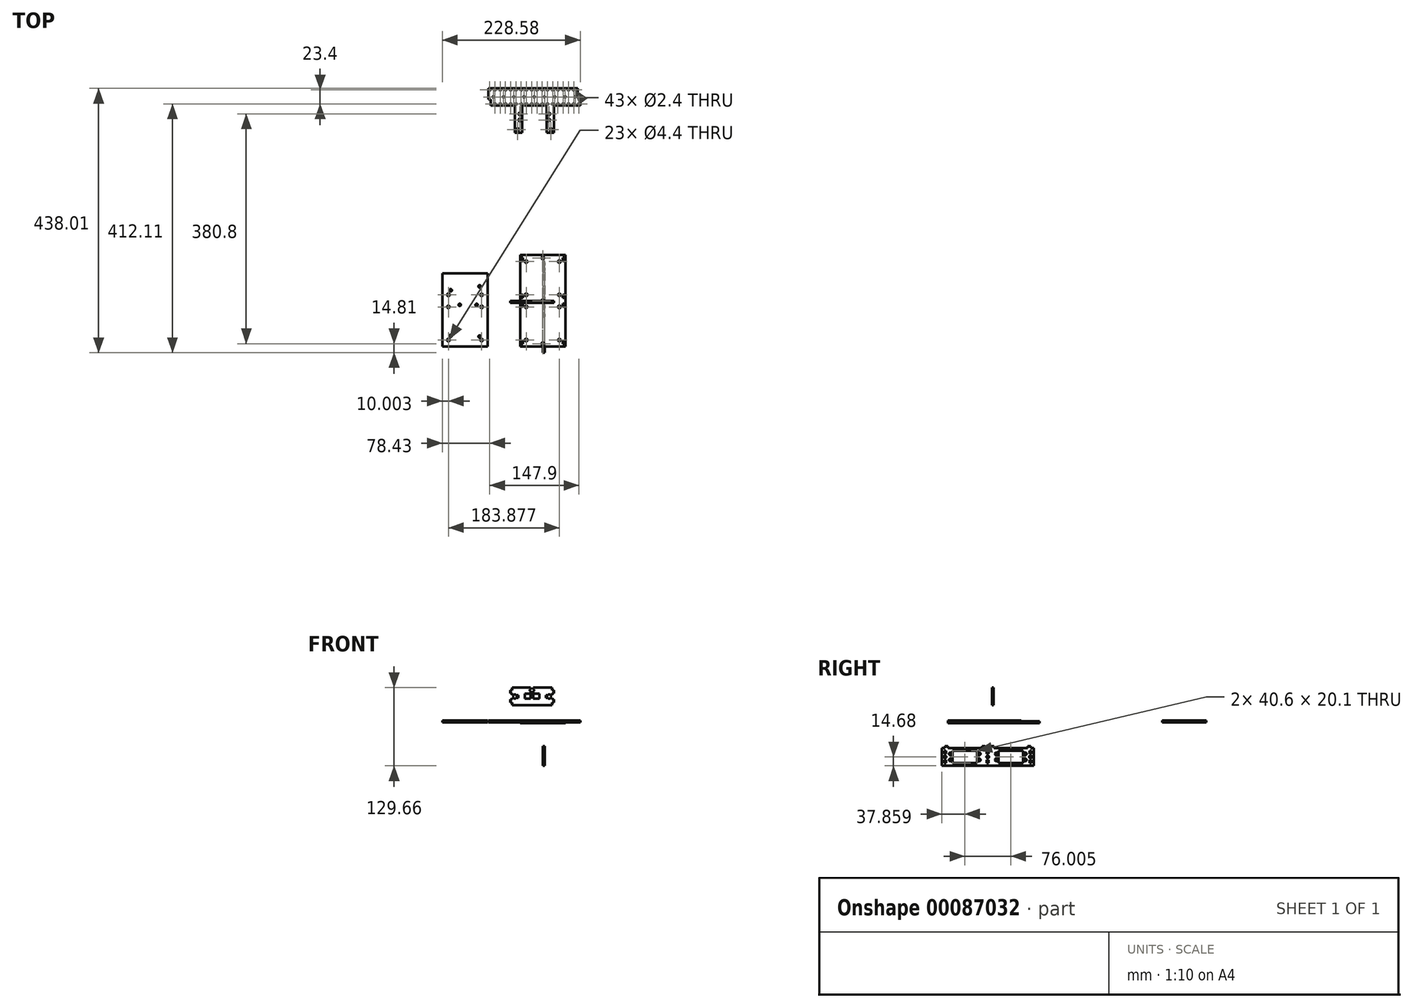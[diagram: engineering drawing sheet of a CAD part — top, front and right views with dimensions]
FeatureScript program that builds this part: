
annotation { "Feature Type Name" : "Feature", "Feature Type Description" : "" }
export const myFeature = defineFeature(function(context is Context, id is Id, definition is map)
    precondition{}
    {
        {
            assignVariable(context, id + "F0", {"name" : "Mat_Thickness", "anyValue" : 3});
        }
        {
            var Q0;
            Q0=qCreatedBy(makeId("Top.planeOp"),FACE);
            var sketch = newSketch(context, id + "F1", { "sketchPlane" : qUnion([Q0])});
            skLineSegment(sketch, "E0.bottom", {"start": v(-37.5, 76) * mm, "end": v(37.5, 76) * mm});
            skLineSegment(sketch, "E0.top", {"start": v(-37.5, -76) * mm, "end": v(37.5, -76) * mm});
            skLineSegment(sketch, "E0.left", {"start": v(-37.5, 76) * mm, "end": v(-37.5, -76) * mm});
            skLineSegment(sketch, "E0.right", {"start": v(37.5, 76) * mm, "end": v(37.5, -76) * mm});
            skLineSegment(sketch, "E1", {"start": v(-37.5, -76) * mm, "end": v(37.5, 76) * mm, "construction": true});
            skLineSegment(sketch, "E2", {"start": v(-37.5, 76) * mm, "end": v(37.5, -76) * mm, "construction": true});
            skSolve(sketch);
        }
        {
            var Q0;
            Q0=makeQuery(id+"F1.imprint","IMPRINT",FACE,{"disambiguationData":[TD([[makeQuery(id+"F1.imprint","IMPRINT",EDGE,{"derivedFrom":sQuery(id+"F1.wireOp",EDGE,"E0.bottom")}),-1.0]])]});
            extrude(context, id + "F2", {"entities" : qUnion([Q0]), "endBound" : BoundingType.SYMMETRIC, "depth" : 3 * mm});
        }
        {
            var Q0;
            Q0=makeQuery(id+"F2.opExtrude","CAP_FACE",FACE,{"disambiguationData":[OSD([sQuery(id+"F1.wireOp",EDGE,"E0.bottom"),sQuery(id+"F1.wireOp",EDGE,"E0.top"),sQuery(id+"F1.wireOp",EDGE,"E0.left"),sQuery(id+"F1.wireOp",EDGE,"E0.right")])],"isStart":false});
            var sketch = newSketch(context, id + "F3", { "sketchPlane" : qUnion([Q0])});
            skPoint(sketch, "E3", {"position": v(-27.5, -71) * mm});
            skPoint(sketch, "E4", {"position": v(27.5, -71) * mm});
            skPoint(sketch, "E5", {"position": v(27.5, 71) * mm});
            skPoint(sketch, "E6", {"position": v(-27.5, 71) * mm});
            skLineSegment(sketch, "E7", {"start": v(-27.5, -71) * mm, "end": v(-27.5, 0) * mm, "construction": true});
            skLineSegment(sketch, "E8", {"start": v(-27.5, 0) * mm, "end": v(-27.5, 71) * mm, "construction": true});
            skLineSegment(sketch, "E9", {"start": v(-27.5, 71) * mm, "end": v(27.5, 71) * mm, "construction": true});
            skLineSegment(sketch, "E10", {"start": v(27.5, 71) * mm, "end": v(27.5, 0) * mm, "construction": true});
            skLineSegment(sketch, "E11", {"start": v(27.5, 0) * mm, "end": v(27.5, -71) * mm, "construction": true});
            skLineSegment(sketch, "E12", {"start": v(27.5, -71) * mm, "end": v(-27.5, -71) * mm, "construction": true});
            skLineSegment(sketch, "E13", {"start": v(-27.5, 0) * mm, "end": v(27.5, 0) * mm, "construction": true});
            skPoint(sketch, "E14", {"position": v(0, 0) * mm});
            skPoint(sketch, "E15", {"position": v(0, 71) * mm});
            skPoint(sketch, "E16", {"position": v(0, -71) * mm});
            skLineSegment(sketch, "E17", {"start": v(27.5, -10) * mm, "end": v(-27.5, -10) * mm, "construction": true});
            skLineSegment(sketch, "E18", {"start": v(27.5, 10) * mm, "end": v(-27.5, 10) * mm, "construction": true});
            skPoint(sketch, "E19", {"position": v(27.5, -10) * mm});
            skPoint(sketch, "E20", {"position": v(27.5, 10) * mm});
            skPoint(sketch, "E21", {"position": v(-27.5, 10) * mm});
            skPoint(sketch, "E22", {"position": v(-27.5, -10) * mm});
            skLineSegment(sketch, "E23.bottom", {"start": v(-27.5, -65) * mm, "end": v(27.5, -65) * mm, "construction": true});
            skLineSegment(sketch, "E23.top", {"start": v(-27.5, 65) * mm, "end": v(27.5, 65) * mm, "construction": true});
            skLineSegment(sketch, "E23.left", {"start": v(-27.5, -65) * mm, "end": v(-27.5, 65) * mm, "construction": true});
            skLineSegment(sketch, "E23.right", {"start": v(27.5, -65) * mm, "end": v(27.5, 65) * mm, "construction": true});
            skSolve(sketch);
        }
        {
            var Q0;
            Q0=sQuery(id+"F3.wireOp",VERTEX,"E14");
            var Q1;
            Q1=sQuery(id+"F3.wireOp",VERTEX,"E15");
            var Q2;
            Q2=sQuery(id+"F3.wireOp",VERTEX,"E16");
            var Q3;
            Q3=sQuery(id+"F3.wireOp",VERTEX,"E20");
            var Q4;
            Q4=sQuery(id+"F3.wireOp",VERTEX,"E19");
            var Q5;
            Q5=sQuery(id+"F3.wireOp",VERTEX,"E22");
            var Q6;
            Q6=sQuery(id+"F3.wireOp",VERTEX,"E21");
            var Q7;
            Q7=sQuery(id+"F3.wireOp",VERTEX,"E23.left.end");
            var Q8;
            Q8=sQuery(id+"F3.wireOp",VERTEX,"E23.right.end");
            var Q9;
            Q9=sQuery(id+"F3.wireOp",VERTEX,"E23.bottom.start");
            var Q10;
            Q10=sQuery(id+"F3.wireOp",VERTEX,"E23.right.start");
            var Q11;
            Q11=makeQuery(id+"F2.opExtrude","SWEPT_BODY",BODY,{"disambiguationData":[OSD([sQuery(id+"F1.wireOp",EDGE,"E0.bottom"),sQuery(id+"F1.wireOp",EDGE,"E0.top"),sQuery(id+"F1.wireOp",EDGE,"E0.left"),sQuery(id+"F1.wireOp",EDGE,"E0.right")])]});
            hole(context, id + "F4", {"style" : HoleStyle.SIMPLE, "endStyle" : HoleEndStyle.THROUGH, "standardTappedOrClearance" : lookupTablePath({ "standard" : "ISO", "fit" : "Normal", "size" : "M4", "type" : "Clearance" }), "standardBlindInLast" : lookupTablePath({ "fit" : "Standard", "standard" : "ISO", "size" : "M4", "type" : "Clearance" }), "holeDiameter" : 4.4 * mm, "locations" : qUnion([Q0, Q1, Q2, Q3, Q4, Q5, Q6, Q7, Q8, Q9, Q10]), "scope" : qUnion([Q11]), "isTappedThrough" : true});
        }
        {
            var Q0;
            Q0=qCreatedBy(makeId("Right.planeOp"),FACE);
            var sketch = newSketch(context, id + "F5", { "sketchPlane" : qUnion([Q0])});
            skLineSegment(sketch, "E24.bottom", {"start": v(-85.81, -72.16) * mm, "end": v(66.19, -72.16) * mm});
            skLineSegment(sketch, "E24.left", {"start": v(-85.81, -72.16) * mm, "end": v(-85.81, -42.8) * mm});
            skLineSegment(sketch, "E24.right", {"start": v(66.19, -72.16) * mm, "end": v(66.19, -42.8) * mm});
            skLineSegment(sketch, "E25", {"start": v(-85.81, -42.8) * mm, "end": v(-81.11, -42.8) * mm});
            skLineSegment(sketch, "E26", {"start": v(-81.11, -42.8) * mm, "end": v(-81.11, -39.8) * mm});
            skLineSegment(sketch, "E27", {"start": v(-81.11, -39.8) * mm, "end": v(-75.91, -39.8) * mm});
            skLineSegment(sketch, "E28", {"start": v(-75.91, -39.8) * mm, "end": v(-75.91, -42.8) * mm});
            skLineSegment(sketch, "E29", {"start": v(-75.91, -42.8) * mm, "end": v(-19.71, -42.8) * mm});
            skLineSegment(sketch, "E30", {"start": v(-19.71, -42.8) * mm, "end": v(-19.71, -39.8) * mm});
            skLineSegment(sketch, "E31", {"start": v(-19.71, -39.8) * mm, "end": v(-14.51, -39.8) * mm});
            skLineSegment(sketch, "E32", {"start": v(-14.51, -39.8) * mm, "end": v(-14.51, -42.8) * mm});
            skLineSegment(sketch, "E33", {"start": v(-14.51, -42.8) * mm, "end": v(-5.11, -42.8) * mm});
            skLineSegment(sketch, "E34", {"start": v(-5.11, -42.8) * mm, "end": v(-5.11, -39.8) * mm});
            skLineSegment(sketch, "E35", {"start": v(-5.11, -39.8) * mm, "end": v(0.09, -39.8) * mm});
            skLineSegment(sketch, "E36", {"start": v(0.09, -39.8) * mm, "end": v(0.09, -42.8) * mm});
            skLineSegment(sketch, "E37", {"start": v(0.09, -42.8) * mm, "end": v(56.29, -42.8) * mm});
            skLineSegment(sketch, "E38", {"start": v(56.29, -42.8) * mm, "end": v(56.29, -39.8) * mm});
            skLineSegment(sketch, "E39", {"start": v(56.29, -39.8) * mm, "end": v(61.49, -39.8) * mm});
            skLineSegment(sketch, "E40", {"start": v(61.49, -39.8) * mm, "end": v(61.49, -42.8) * mm});
            skLineSegment(sketch, "E41", {"start": v(61.49, -42.8) * mm, "end": v(66.19, -42.8) * mm});
            skPoint(sketch, "E42", {"position": v(-9.95, -72.16) * mm});
            skPoint(sketch, "E42.positionSnap0", {"position": v(-9.81, -72.16) * mm});
            skLineSegment(sketch, "E43", {"start": v(-9.95, -72.16) * mm, "end": v(-9.95, -42.8) * mm, "construction": true});
            skLineSegment(sketch, "E44.bottom", {"start": v(-68.25, -47.43) * mm, "end": v(-27.65, -47.43) * mm});
            skLineSegment(sketch, "E44.top", {"start": v(-68.25, -67.53) * mm, "end": v(-27.65, -67.53) * mm});
            skLineSegment(sketch, "E44.left", {"start": v(-68.25, -47.43) * mm, "end": v(-68.25, -67.53) * mm});
            skLineSegment(sketch, "E44.right", {"start": v(-27.65, -47.43) * mm, "end": v(-27.65, -67.53) * mm});
            skCircle(sketch, "E45", {"center": v(-71.95, -52.48) * mm, "radius": 2.2 * mm});
            skCircle(sketch, "E46", {"center": v(-23.95, -52.48) * mm, "radius": 2.2 * mm});
            skCircle(sketch, "E47", {"center": v(-23.95, -62.48) * mm, "radius": 2.2 * mm});
            skCircle(sketch, "E48", {"center": v(-71.95, -62.48) * mm, "radius": 2.2 * mm});
            skLineSegment(sketch, "E49.bottom", {"start": v(-71.95, -52.48) * mm, "end": v(-23.95, -52.48) * mm, "construction": true});
            skLineSegment(sketch, "E49.top", {"start": v(-71.95, -62.48) * mm, "end": v(-23.95, -62.48) * mm, "construction": true});
            skLineSegment(sketch, "E49.left", {"start": v(-71.95, -52.48) * mm, "end": v(-71.95, -62.48) * mm, "construction": true});
            skLineSegment(sketch, "E49.right", {"start": v(-23.95, -52.48) * mm, "end": v(-23.95, -62.48) * mm, "construction": true});
            skCircle(sketch, "E50.MirrorC", {"center": v(4.05, -52.48) * mm, "radius": 2.2 * mm});
            skCircle(sketch, "E51.MirrorC", {"center": v(4.05, -62.48) * mm, "radius": 2.2 * mm});
            skLineSegment(sketch, "E52.MirrorCS", {"start": v(7.75, -47.43) * mm, "end": v(7.75, -67.53) * mm});
            skLineSegment(sketch, "E53.MirrorCS", {"start": v(48.35, -47.43) * mm, "end": v(7.75, -47.43) * mm});
            skLineSegment(sketch, "E54.MirrorCS", {"start": v(48.35, -47.43) * mm, "end": v(48.35, -67.53) * mm});
            skLineSegment(sketch, "E55.MirrorCS", {"start": v(48.35, -67.53) * mm, "end": v(7.75, -67.53) * mm});
            skCircle(sketch, "E56.MirrorC", {"center": v(52.05, -62.48) * mm, "radius": 2.2 * mm});
            skCircle(sketch, "E57.MirrorC", {"center": v(52.05, -52.48) * mm, "radius": 2.2 * mm});
            skCircle(sketch, "E58", {"center": v(-9.95, -57.48) * mm, "radius": 2.2 * mm});
            skLineSegment(sketch, "E59.bottom", {"start": v(-11.45, -52.48) * mm, "end": v(-8.45, -52.48) * mm});
            skLineSegment(sketch, "E59.top", {"start": v(-11.45, -47.18) * mm, "end": v(-8.45, -47.18) * mm});
            skLineSegment(sketch, "E59.left", {"start": v(-11.45, -52.48) * mm, "end": v(-11.45, -47.18) * mm});
            skLineSegment(sketch, "E59.right", {"start": v(-8.45, -52.48) * mm, "end": v(-8.45, -47.18) * mm});
            skPoint(sketch, "E59.middle", {"position": v(-9.95, -49.83) * mm});
            skLineSegment(sketch, "E60.bottom", {"start": v(-11.45, -67.78) * mm, "end": v(-8.45, -67.78) * mm});
            skLineSegment(sketch, "E60.top", {"start": v(-11.45, -62.48) * mm, "end": v(-8.45, -62.48) * mm});
            skLineSegment(sketch, "E60.left", {"start": v(-11.45, -67.78) * mm, "end": v(-11.45, -62.48) * mm});
            skLineSegment(sketch, "E60.right", {"start": v(-8.45, -67.78) * mm, "end": v(-8.45, -62.48) * mm});
            skPoint(sketch, "E60.middle", {"position": v(-9.95, -65.13) * mm});
            skLineSegment(sketch, "E61.bottom", {"start": v(62.42, -47.18) * mm, "end": v(59.42, -47.18) * mm});
            skLineSegment(sketch, "E61.top", {"start": v(62.42, -52.48) * mm, "end": v(59.42, -52.48) * mm});
            skLineSegment(sketch, "E61.left", {"start": v(62.42, -47.18) * mm, "end": v(62.42, -52.48) * mm});
            skLineSegment(sketch, "E61.right", {"start": v(59.42, -47.18) * mm, "end": v(59.42, -52.48) * mm});
            skLineSegment(sketch, "E62.bottom", {"start": v(62.42, -67.78) * mm, "end": v(59.42, -67.78) * mm});
            skLineSegment(sketch, "E62.top", {"start": v(62.42, -62.48) * mm, "end": v(59.42, -62.48) * mm});
            skLineSegment(sketch, "E62.left", {"start": v(62.42, -67.78) * mm, "end": v(62.42, -62.48) * mm});
            skLineSegment(sketch, "E62.right", {"start": v(59.42, -67.78) * mm, "end": v(59.42, -62.48) * mm});
            skLineSegment(sketch, "E63", {"start": v(66.19, -57.48) * mm, "end": v(-85.81, -57.48) * mm, "construction": true});
            skPoint(sketch, "E64", {"position": v(48.35, -57.48) * mm});
            skLineSegment(sketch, "E65", {"start": v(-68.25, -67.53) * mm, "end": v(-27.65, -47.43) * mm, "construction": true});
            skPoint(sketch, "E66", {"position": v(-47.95, -57.48) * mm});
            skCircle(sketch, "E67", {"center": v(60.92, -57.48) * mm, "radius": 2.2 * mm});
            skPoint(sketch, "E67.centerSnap0", {"position": v(60.92, -52.48) * mm});
            skCircle(sketch, "E68.MirrorC", {"center": v(-80.81, -57.48) * mm, "radius": 2.2 * mm});
            skLineSegment(sketch, "E69.MirrorCS", {"start": v(-82.31, -52.48) * mm, "end": v(-79.31, -52.48) * mm});
            skLineSegment(sketch, "E70.MirrorCS", {"start": v(-82.31, -47.18) * mm, "end": v(-79.31, -47.18) * mm});
            skLineSegment(sketch, "E71.MirrorCS", {"start": v(-82.31, -47.18) * mm, "end": v(-82.31, -52.48) * mm});
            skLineSegment(sketch, "E72.MirrorCS", {"start": v(-79.31, -47.18) * mm, "end": v(-79.31, -52.48) * mm});
            skLineSegment(sketch, "E73.MirrorCS", {"start": v(-82.31, -67.78) * mm, "end": v(-82.31, -62.48) * mm});
            skLineSegment(sketch, "E74.MirrorCS", {"start": v(-82.31, -62.48) * mm, "end": v(-79.31, -62.48) * mm});
            skLineSegment(sketch, "E75.MirrorCS", {"start": v(-86.08, -57.48) * mm, "end": v(65.92, -57.48) * mm, "construction": true});
            skLineSegment(sketch, "E76.MirrorCS", {"start": v(-79.31, -67.78) * mm, "end": v(-79.31, -62.48) * mm});
            skLineSegment(sketch, "E77.MirrorCS", {"start": v(-82.31, -67.78) * mm, "end": v(-79.31, -67.78) * mm});
            skLineSegment(sketch, "E78.bottom", {"start": v(52.05, -52.48) * mm, "end": v(4.05, -52.48) * mm, "construction": true});
            skLineSegment(sketch, "E78.top", {"start": v(52.05, -62.48) * mm, "end": v(4.05, -62.48) * mm, "construction": true});
            skLineSegment(sketch, "E78.left", {"start": v(52.05, -52.48) * mm, "end": v(52.05, -62.48) * mm, "construction": true});
            skLineSegment(sketch, "E78.right", {"start": v(4.05, -52.48) * mm, "end": v(4.05, -62.48) * mm, "construction": true});
            skPoint(sketch, "E79", {"position": v(-71.95, -57.48) * mm});
            skLineSegment(sketch, "E80", {"start": v(28.05, -52.48) * mm, "end": v(28.05, -62.48) * mm, "construction": true});
            skLineSegment(sketch, "E81", {"start": v(-47.95, -52.48) * mm, "end": v(-47.95, -57.48) * mm, "construction": true});
            skSolve(sketch);
        }
        {
            var Q0;
            Q0 = qSketchRegion(id + "F5", true);
            extrude(context, id + "F6", {"entities" : qUnion([Q0]), "depth" : (getVariable(context, 'Mat_Thickness')) * mm});
        }
        {
            var Q0;
            Q0=qCreatedBy(makeId("Front.planeOp"),FACE);
            var sketch = newSketch(context, id + "F7", { "sketchPlane" : qUnion([Q0])});
            skLineSegment(sketch, "E82", {"start": v(-50.74, 45.02) * mm, "end": v(-47.74, 45.02) * mm});
            skLineSegment(sketch, "E83", {"start": v(-47.74, 45.02) * mm, "end": v(-47.74, 46.32) * mm});
            skLineSegment(sketch, "E84", {"start": v(-47.74, 46.32) * mm, "end": v(-44.74, 46.32) * mm});
            skLineSegment(sketch, "E85", {"start": v(-44.74, 46.32) * mm, "end": v(-44.74, 45.02) * mm});
            skLineSegment(sketch, "E86", {"start": v(-44.74, 45.02) * mm, "end": v(-40.74, 45.02) * mm});
            skLineSegment(sketch, "E87", {"start": v(-40.74, 45.02) * mm, "end": v(-40.74, 40.62) * mm});
            skLineSegment(sketch, "E88", {"start": v(-40.74, 40.62) * mm, "end": v(-44.74, 40.62) * mm});
            skLineSegment(sketch, "E89", {"start": v(-44.74, 40.62) * mm, "end": v(-44.74, 39.32) * mm});
            skLineSegment(sketch, "E90", {"start": v(-44.74, 39.32) * mm, "end": v(-47.74, 39.32) * mm});
            skLineSegment(sketch, "E91", {"start": v(-47.74, 39.32) * mm, "end": v(-47.74, 40.62) * mm});
            skLineSegment(sketch, "E92", {"start": v(-47.74, 40.62) * mm, "end": v(-50.74, 40.62) * mm});
            skLineSegment(sketch, "E93", {"start": v(-17.74, 57.5) * mm, "end": v(-17.74, 28.15) * mm, "construction": true});
            skLineSegment(sketch, "E94", {"start": v(-50.74, 28.15) * mm, "end": v(-17.74, 28.15) * mm});
            skLineSegment(sketch, "E95", {"start": v(-50.74, 57.5) * mm, "end": v(-50.74, 53.07) * mm});
            skLineSegment(sketch, "E96", {"start": v(-50.74, 28.15) * mm, "end": v(-50.74, 32.57) * mm});
            skLineSegment(sketch, "E97", {"start": v(-19.94, 48.5) * mm, "end": v(-19.94, 51.5) * mm});
            skLineSegment(sketch, "E98", {"start": v(-19.94, 51.5) * mm, "end": v(-21.24, 51.5) * mm});
            skLineSegment(sketch, "E99", {"start": v(-21.24, 51.5) * mm, "end": v(-21.24, 54.5) * mm});
            skLineSegment(sketch, "E100", {"start": v(-21.24, 54.5) * mm, "end": v(-19.94, 54.5) * mm});
            skLineSegment(sketch, "E101", {"start": v(-19.94, 54.5) * mm, "end": v(-19.94, 57.5) * mm});
            skLineSegment(sketch, "E102", {"start": v(-50.74, 57.5) * mm, "end": v(-19.94, 57.5) * mm});
            skLineSegment(sketch, "E103", {"start": v(-19.94, 48.5) * mm, "end": v(-17.74, 48.5) * mm});
            skLineSegment(sketch, "E104", {"start": v(-50.74, 45.02) * mm, "end": v(-50.74, 40.62) * mm, "construction": true});
            skLineSegment(sketch, "E105", {"start": v(-40.74, 42.82) * mm, "end": v(-50.74, 42.82) * mm, "construction": true});
            skLineSegment(sketch, "E106", {"start": v(-50.74, 47.87) * mm, "end": v(-53.74, 47.87) * mm});
            skLineSegment(sketch, "E107", {"start": v(-53.74, 47.87) * mm, "end": v(-53.74, 53.07) * mm});
            skLineSegment(sketch, "E108", {"start": v(-53.74, 53.07) * mm, "end": v(-50.74, 53.07) * mm});
            skLineSegment(sketch, "E109.trimOffspring", {"start": v(-50.74, 47.87) * mm, "end": v(-50.74, 45.02) * mm});
            skLineSegment(sketch, "E110", {"start": v(-50.74, 37.77) * mm, "end": v(-53.74, 37.77) * mm});
            skLineSegment(sketch, "E111", {"start": v(-53.74, 37.77) * mm, "end": v(-53.74, 32.57) * mm});
            skLineSegment(sketch, "E112", {"start": v(-53.74, 32.57) * mm, "end": v(-50.74, 32.57) * mm});
            skLineSegment(sketch, "E113.trimOffspring", {"start": v(-50.74, 37.77) * mm, "end": v(-50.74, 40.62) * mm});
            skLineSegment(sketch, "E114.MirrorCS", {"start": v(9.26, 46.32) * mm, "end": v(9.26, 45.02) * mm});
            skLineSegment(sketch, "E115.MirrorCS", {"start": v(9.26, 40.62) * mm, "end": v(9.26, 39.32) * mm});
            skLineSegment(sketch, "E116.MirrorCS", {"start": v(12.26, 45.02) * mm, "end": v(12.26, 46.32) * mm});
            skLineSegment(sketch, "E117.MirrorCS", {"start": v(9.26, 45.02) * mm, "end": v(5.26, 45.02) * mm});
            skLineSegment(sketch, "E118.MirrorCS", {"start": v(12.26, 39.32) * mm, "end": v(12.26, 40.62) * mm});
            skLineSegment(sketch, "E119.MirrorCS", {"start": v(-15.54, 51.5) * mm, "end": v(-14.24, 51.5) * mm});
            skLineSegment(sketch, "E120.MirrorCS", {"start": v(-14.24, 54.5) * mm, "end": v(-15.54, 54.5) * mm});
            skLineSegment(sketch, "E121.MirrorCS", {"start": v(5.26, 40.62) * mm, "end": v(9.26, 40.62) * mm});
            skLineSegment(sketch, "E122.MirrorCS", {"start": v(-15.54, 48.5) * mm, "end": v(-15.54, 51.5) * mm});
            skLineSegment(sketch, "E123.MirrorCS", {"start": v(-15.54, 48.5) * mm, "end": v(-17.74, 48.5) * mm});
            skLineSegment(sketch, "E124.MirrorCS", {"start": v(15.26, 45.02) * mm, "end": v(15.26, 40.62) * mm, "construction": true});
            skLineSegment(sketch, "E125.MirrorCS", {"start": v(5.26, 45.02) * mm, "end": v(5.26, 40.62) * mm});
            skLineSegment(sketch, "E126.MirrorCS", {"start": v(15.26, 45.02) * mm, "end": v(12.26, 45.02) * mm});
            skLineSegment(sketch, "E127.MirrorCS", {"start": v(18.26, 32.57) * mm, "end": v(15.26, 32.57) * mm});
            skLineSegment(sketch, "E128.MirrorCS", {"start": v(18.26, 37.77) * mm, "end": v(18.26, 32.57) * mm});
            skLineSegment(sketch, "E129.MirrorCS", {"start": v(5.26, 42.82) * mm, "end": v(15.26, 42.82) * mm, "construction": true});
            skLineSegment(sketch, "E130.MirrorCS", {"start": v(15.26, 37.77) * mm, "end": v(15.26, 40.62) * mm});
            skLineSegment(sketch, "E131.MirrorCS", {"start": v(15.26, 37.77) * mm, "end": v(18.26, 37.77) * mm});
            skLineSegment(sketch, "E132.MirrorCS", {"start": v(12.26, 40.62) * mm, "end": v(15.26, 40.62) * mm});
            skLineSegment(sketch, "E133.MirrorCS", {"start": v(15.26, 28.15) * mm, "end": v(-17.74, 28.15) * mm});
            skLineSegment(sketch, "E134.MirrorCS", {"start": v(-14.24, 51.5) * mm, "end": v(-14.24, 54.5) * mm});
            skLineSegment(sketch, "E135.MirrorCS", {"start": v(-15.54, 54.5) * mm, "end": v(-15.54, 57.5) * mm});
            skLineSegment(sketch, "E136.MirrorCS", {"start": v(9.26, 39.32) * mm, "end": v(12.26, 39.32) * mm});
            skLineSegment(sketch, "E137.MirrorCS", {"start": v(15.26, 57.5) * mm, "end": v(-15.54, 57.5) * mm});
            skLineSegment(sketch, "E138.MirrorCS", {"start": v(15.26, 47.87) * mm, "end": v(15.26, 45.02) * mm});
            skLineSegment(sketch, "E139.MirrorCS", {"start": v(15.26, 57.5) * mm, "end": v(15.26, 53.07) * mm});
            skLineSegment(sketch, "E140.MirrorCS", {"start": v(15.26, 47.87) * mm, "end": v(18.26, 47.87) * mm});
            skLineSegment(sketch, "E141.MirrorCS", {"start": v(18.26, 47.87) * mm, "end": v(18.26, 53.07) * mm});
            skLineSegment(sketch, "E142.MirrorCS", {"start": v(15.26, 28.15) * mm, "end": v(15.26, 32.57) * mm});
            skLineSegment(sketch, "E143.MirrorCS", {"start": v(18.26, 53.07) * mm, "end": v(15.26, 53.07) * mm});
            skLineSegment(sketch, "E144.MirrorCS", {"start": v(12.26, 46.32) * mm, "end": v(9.26, 46.32) * mm});
            skLineSegment(sketch, "E145.bottom", {"start": v(-29.94, 47.19) * mm, "end": v(-19.94, 47.19) * mm});
            skLineSegment(sketch, "E145.top", {"start": v(-29.94, 39.26) * mm, "end": v(-19.94, 39.26) * mm});
            skLineSegment(sketch, "E145.left", {"start": v(-29.94, 47.19) * mm, "end": v(-29.94, 39.26) * mm});
            skLineSegment(sketch, "E145.right", {"start": v(-19.94, 47.19) * mm, "end": v(-19.94, 39.26) * mm});
            skLineSegment(sketch, "E146.MirrorCS", {"start": v(-5.54, 47.19) * mm, "end": v(-15.54, 47.19) * mm});
            skLineSegment(sketch, "E147.MirrorCS", {"start": v(-5.54, 47.19) * mm, "end": v(-5.54, 39.26) * mm});
            skLineSegment(sketch, "E148.MirrorCS", {"start": v(-5.54, 39.26) * mm, "end": v(-15.54, 39.26) * mm});
            skLineSegment(sketch, "E149.MirrorCS", {"start": v(-15.54, 47.19) * mm, "end": v(-15.54, 39.26) * mm});
            skSolve(sketch);
        }
        {
            var Q0;
            Q0=makeQuery(id+"F2.opExtrude","CAP_FACE",FACE,{"disambiguationData":[OSD([sQuery(id+"F1.wireOp",EDGE,"E0.bottom"),sQuery(id+"F1.wireOp",EDGE,"E0.top"),sQuery(id+"F1.wireOp",EDGE,"E0.left"),sQuery(id+"F1.wireOp",EDGE,"E0.right")])],"isStart":false});
            var sketch = newSketch(context, id + "F8", { "sketchPlane" : qUnion([Q0])});
            skLineSegment(sketch, "E150.bottom", {"start": v(36, -71.35) * mm, "end": v(33, -71.35) * mm});
            skLineSegment(sketch, "E150.top", {"start": v(36, -66.05) * mm, "end": v(33, -66.05) * mm});
            skLineSegment(sketch, "E150.left", {"start": v(36, -71.35) * mm, "end": v(36, -66.05) * mm});
            skLineSegment(sketch, "E150.right", {"start": v(33, -71.35) * mm, "end": v(33, -66.05) * mm});
            skLineSegment(sketch, "E151.bottom", {"start": v(36, -9.95) * mm, "end": v(33, -9.95) * mm});
            skLineSegment(sketch, "E151.top", {"start": v(36, -4.65) * mm, "end": v(33, -4.65) * mm});
            skLineSegment(sketch, "E151.left", {"start": v(36, -9.95) * mm, "end": v(36, -4.65) * mm});
            skLineSegment(sketch, "E151.right", {"start": v(33, -9.95) * mm, "end": v(33, -4.65) * mm});
            skLineSegment(sketch, "E152.bottom", {"start": v(36, 4.65) * mm, "end": v(33, 4.65) * mm});
            skLineSegment(sketch, "E152.top", {"start": v(36, 9.95) * mm, "end": v(33, 9.95) * mm});
            skLineSegment(sketch, "E152.left", {"start": v(36, 4.65) * mm, "end": v(36, 9.95) * mm});
            skLineSegment(sketch, "E152.right", {"start": v(33, 4.65) * mm, "end": v(33, 9.95) * mm});
            skLineSegment(sketch, "E153.bottom", {"start": v(36, 66.05) * mm, "end": v(33, 66.05) * mm});
            skLineSegment(sketch, "E153.top", {"start": v(36, 71.35) * mm, "end": v(33, 71.35) * mm});
            skLineSegment(sketch, "E153.left", {"start": v(36, 66.05) * mm, "end": v(36, 71.35) * mm});
            skLineSegment(sketch, "E153.right", {"start": v(33, 66.05) * mm, "end": v(33, 71.35) * mm});
            skPoint(sketch, "E154", {"position": v(37.5, 0) * mm});
            skLineSegment(sketch, "E155", {"start": v(0, -76) * mm, "end": v(0, 76) * mm, "construction": true});
            skLineSegment(sketch, "E156.MirrorCS", {"start": v(-36, 9.95) * mm, "end": v(-33, 9.95) * mm});
            skLineSegment(sketch, "E157.MirrorCS", {"start": v(-33, 4.65) * mm, "end": v(-33, 9.95) * mm});
            skLineSegment(sketch, "E158.MirrorCS", {"start": v(-36, 4.65) * mm, "end": v(-36, 9.95) * mm});
            skLineSegment(sketch, "E159.MirrorCS", {"start": v(-36, 4.65) * mm, "end": v(-33, 4.65) * mm});
            skLineSegment(sketch, "E160.MirrorCS", {"start": v(-36, 66.05) * mm, "end": v(-36, 71.35) * mm});
            skLineSegment(sketch, "E161.MirrorCS", {"start": v(-36, 66.05) * mm, "end": v(-33, 66.05) * mm});
            skLineSegment(sketch, "E162.MirrorCS", {"start": v(-33, -9.95) * mm, "end": v(-33, -4.65) * mm});
            skLineSegment(sketch, "E163.MirrorCS", {"start": v(-36, -9.95) * mm, "end": v(-36, -4.65) * mm});
            skLineSegment(sketch, "E164.MirrorCS", {"start": v(-36, -4.65) * mm, "end": v(-33, -4.65) * mm});
            skLineSegment(sketch, "E165.MirrorCS", {"start": v(-33, -71.35) * mm, "end": v(-33, -66.05) * mm});
            skLineSegment(sketch, "E166.MirrorCS", {"start": v(-36, -66.05) * mm, "end": v(-33, -66.05) * mm});
            skLineSegment(sketch, "E167.MirrorCS", {"start": v(-36, -9.95) * mm, "end": v(-33, -9.95) * mm});
            skLineSegment(sketch, "E168.MirrorCS", {"start": v(-33, 66.05) * mm, "end": v(-33, 71.35) * mm});
            skLineSegment(sketch, "E169.MirrorCS", {"start": v(-36, -71.35) * mm, "end": v(-36, -66.05) * mm});
            skLineSegment(sketch, "E170.MirrorCS", {"start": v(-36, 71.35) * mm, "end": v(-33, 71.35) * mm});
            skLineSegment(sketch, "E171.MirrorCS", {"start": v(-36, -71.35) * mm, "end": v(-33, -71.35) * mm});
            skPoint(sketch, "E172.MirrorP", {"position": v(-37.5, 0) * mm});
            skSolve(sketch);
        }
        {
            var Q0;
            Q0 = qSketchRegion(id + "F8", true);
            extrude(context, id + "F9", {"entities" : qUnion([Q0]), "operationType" : NewBodyOperationType.REMOVE, "oppositeDirection" : true, "depth" : 25 * mm});
        }
        {
            var Q0;
            Q0=makeQuery(id+"F7.imprint","IMPRINT",FACE,{"disambiguationData":[TD([[makeQuery(id+"F7.imprint","IMPRINT",EDGE,{"derivedFrom":sQuery(id+"F7.wireOp",EDGE,"E82")}),1.0]])]});
            extrude(context, id + "F10", {"entities" : qUnion([Q0]), "depth" : (getVariable(context, 'Mat_Thickness')) * mm});
        }
        {
            var Q0;
            Q0=makeQuery(id+"F2.opExtrude","CAP_FACE",FACE,{"disambiguationData":[OSD([sQuery(id+"F1.wireOp",EDGE,"E0.bottom"),sQuery(id+"F1.wireOp",EDGE,"E0.top"),sQuery(id+"F1.wireOp",EDGE,"E0.left"),sQuery(id+"F1.wireOp",EDGE,"E0.right")])],"isStart":false});
            var sketch = newSketch(context, id + "F11", { "sketchPlane" : qUnion([Q0])});
            skLineSegment(sketch, "E173", {"start": v(24, 63.8) * mm, "end": v(-24, 63.8) * mm, "construction": true});
            skLineSegment(sketch, "E174", {"start": v(-24, 63.8) * mm, "end": v(-37.5, 63.8) * mm, "construction": true});
            skLineSegment(sketch, "E175", {"start": v(24, 63.8) * mm, "end": v(37.5, 63.8) * mm, "construction": true});
            skSolve(sketch);
        }
        {
            var Q0;
            Q0=qCreatedBy(makeId("Top.planeOp"),FACE);
            var sketch = newSketch(context, id + "F12", { "sketchPlane" : qUnion([Q0])});
            skLineSegment(sketch, "E176", {"start": v(6.35, 278.8) * mm, "end": v(18.35, 278.8) * mm});
            skLineSegment(sketch, "E177", {"start": v(-46.35, 278.8) * mm, "end": v(-34.35, 278.8) * mm});
            skLineSegment(sketch, "E178", {"start": v(-34.35, 278.8) * mm, "end": v(-34.35, 323.8) * mm});
            skLineSegment(sketch, "E179", {"start": v(-34.35, 323.8) * mm, "end": v(6.35, 323.8) * mm});
            skLineSegment(sketch, "E180", {"start": v(62.2, 323.8) * mm, "end": v(62.2, 352.2) * mm});
            skLineSegment(sketch, "E181", {"start": v(62.2, 352.2) * mm, "end": v(-90.2, 352.2) * mm});
            skLineSegment(sketch, "E182", {"start": v(-90.2, 352.2) * mm, "end": v(-90.2, 323.8) * mm});
            skLineSegment(sketch, "E183", {"start": v(-90.2, 323.8) * mm, "end": v(-46.35, 323.8) * mm});
            skLineSegment(sketch, "E184", {"start": v(6.35, 323.8) * mm, "end": v(6.35, 278.8) * mm});
            skLineSegment(sketch, "E185.trimOffspring", {"start": v(18.35, 323.8) * mm, "end": v(62.2, 323.8) * mm});
            skCircle(sketch, "E186", {"center": v(-87.95, 349.7) * mm, "radius": 1.2 * mm});
            skCircle(sketch, "E187", {"center": v(-87.95, 326.3) * mm, "radius": 1.2 * mm});
            skLineSegment(sketch, "E188", {"start": v(-87.95, 349.7) * mm, "end": v(-87.95, 326.3) * mm, "construction": true});
            skCircle(sketch, "E189.1.0.0", {"center": v(-79.25, 349.7) * mm, "radius": 1.2 * mm});
            skCircle(sketch, "E189.1.0.1", {"center": v(-79.25, 326.3) * mm, "radius": 1.2 * mm});
            skCircle(sketch, "E189.2.0.0", {"center": v(-70.55, 349.7) * mm, "radius": 1.2 * mm});
            skCircle(sketch, "E189.2.0.1", {"center": v(-70.55, 326.3) * mm, "radius": 1.2 * mm});
            skCircle(sketch, "E189.3.0.0", {"center": v(-61.85, 349.7) * mm, "radius": 1.2 * mm});
            skCircle(sketch, "E189.3.0.1", {"center": v(-61.85, 326.3) * mm, "radius": 1.2 * mm});
            skCircle(sketch, "E189.4.0.0", {"center": v(-53.15, 349.7) * mm, "radius": 1.2 * mm});
            skCircle(sketch, "E189.4.0.1", {"center": v(-53.15, 326.3) * mm, "radius": 1.2 * mm});
            skCircle(sketch, "E189.5.0.0", {"center": v(-44.45, 349.7) * mm, "radius": 1.2 * mm});
            skCircle(sketch, "E189.5.0.1", {"center": v(-44.45, 326.3) * mm, "radius": 1.2 * mm});
            skCircle(sketch, "E189.6.0.0", {"center": v(-35.75, 349.7) * mm, "radius": 1.2 * mm});
            skCircle(sketch, "E189.6.0.1", {"center": v(-35.75, 326.3) * mm, "radius": 1.2 * mm});
            skCircle(sketch, "E189.7.0.0", {"center": v(-27.05, 349.7) * mm, "radius": 1.2 * mm});
            skCircle(sketch, "E189.7.0.1", {"center": v(-27.05, 326.3) * mm, "radius": 1.2 * mm});
            skCircle(sketch, "E189.8.0.0", {"center": v(-18.35, 349.7) * mm, "radius": 1.2 * mm});
            skCircle(sketch, "E189.8.0.1", {"center": v(-18.35, 326.3) * mm, "radius": 1.2 * mm});
            skCircle(sketch, "E189.9.0.0", {"center": v(-9.65, 349.7) * mm, "radius": 1.2 * mm});
            skCircle(sketch, "E189.9.0.1", {"center": v(-9.65, 326.3) * mm, "radius": 1.2 * mm});
            skCircle(sketch, "E189.10.0.0", {"center": v(-0.95, 349.7) * mm, "radius": 1.2 * mm});
            skCircle(sketch, "E189.10.0.1", {"center": v(-0.95, 326.3) * mm, "radius": 1.2 * mm});
            skCircle(sketch, "E189.11.0.0", {"center": v(7.75, 349.7) * mm, "radius": 1.2 * mm});
            skCircle(sketch, "E189.11.0.1", {"center": v(7.75, 326.3) * mm, "radius": 1.2 * mm});
            skCircle(sketch, "E189.12.0.0", {"center": v(16.45, 349.7) * mm, "radius": 1.2 * mm});
            skCircle(sketch, "E189.12.0.1", {"center": v(16.45, 326.3) * mm, "radius": 1.2 * mm});
            skCircle(sketch, "E189.13.0.0", {"center": v(25.15, 349.7) * mm, "radius": 1.2 * mm});
            skCircle(sketch, "E189.13.0.1", {"center": v(25.15, 326.3) * mm, "radius": 1.2 * mm});
            skCircle(sketch, "E189.14.0.0", {"center": v(33.85, 349.7) * mm, "radius": 1.2 * mm});
            skCircle(sketch, "E189.14.0.1", {"center": v(33.85, 326.3) * mm, "radius": 1.2 * mm});
            skCircle(sketch, "E189.15.0.0", {"center": v(42.55, 349.7) * mm, "radius": 1.2 * mm});
            skCircle(sketch, "E189.15.0.1", {"center": v(42.55, 326.3) * mm, "radius": 1.2 * mm});
            skCircle(sketch, "E189.16.0.0", {"center": v(51.25, 349.7) * mm, "radius": 1.2 * mm});
            skCircle(sketch, "E189.16.0.1", {"center": v(51.25, 326.3) * mm, "radius": 1.2 * mm});
            skCircle(sketch, "E189.17.0.0", {"center": v(59.95, 349.7) * mm, "radius": 1.2 * mm});
            skCircle(sketch, "E189.17.0.1", {"center": v(59.95, 326.3) * mm, "radius": 1.2 * mm});
            skLineSegment(sketch, "E189.direction1", {"start": v(-87.95, 349.7) * mm, "end": v(-79.25, 349.7) * mm, "construction": true});
            skCircle(sketch, "E190", {"center": v(-82, 338) * mm, "radius": 1.2 * mm});
            skCircle(sketch, "E191.1.0.0", {"center": v(-65, 338) * mm, "radius": 1.2 * mm});
            skCircle(sketch, "E191.2.0.0", {"center": v(-48, 338) * mm, "radius": 1.2 * mm});
            skCircle(sketch, "E191.3.0.0", {"center": v(-31, 338) * mm, "radius": 1.2 * mm});
            skCircle(sketch, "E191.4.0.0", {"center": v(-14, 338) * mm, "radius": 1.2 * mm});
            skCircle(sketch, "E191.5.0.0", {"center": v(3, 338) * mm, "radius": 1.2 * mm});
            skCircle(sketch, "E191.6.0.0", {"center": v(20, 338) * mm, "radius": 1.2 * mm});
            skCircle(sketch, "E191.7.0.0", {"center": v(37, 338) * mm, "radius": 1.2 * mm});
            skCircle(sketch, "E191.8.0.0", {"center": v(54, 338) * mm, "radius": 1.2 * mm});
            skLineSegment(sketch, "E191.direction1", {"start": v(-82, 338) * mm, "end": v(-65, 338) * mm, "construction": true});
            skLineSegment(sketch, "E192", {"start": v(-14, 338) * mm, "end": v(-14, 323.8) * mm, "construction": true});
            skLineSegment(sketch, "E193", {"start": v(-9.65, 349.7) * mm, "end": v(-18.35, 326.3) * mm, "construction": true});
            skLineSegment(sketch, "E194.bottom", {"start": v(-38, 309.8) * mm, "end": v(10, 309.8) * mm, "construction": true});
            skLineSegment(sketch, "E194.top", {"start": v(-38, 299.8) * mm, "end": v(10, 299.8) * mm, "construction": true});
            skLineSegment(sketch, "E194.left", {"start": v(-38, 309.8) * mm, "end": v(-38, 299.8) * mm, "construction": true});
            skLineSegment(sketch, "E194.right", {"start": v(10, 309.8) * mm, "end": v(10, 299.8) * mm, "construction": true});
            skCircle(sketch, "E195", {"center": v(-38, 309.8) * mm, "radius": 2.2 * mm});
            skCircle(sketch, "E196", {"center": v(-38, 299.8) * mm, "radius": 2.2 * mm});
            skCircle(sketch, "E197", {"center": v(10, 299.8) * mm, "radius": 2.2 * mm});
            skCircle(sketch, "E198", {"center": v(10, 309.8) * mm, "radius": 2.2 * mm});
            skLineSegment(sketch, "E199", {"start": v(-14, 299.8) * mm, "end": v(-14, 290.1) * mm, "construction": true});
            skLineSegment(sketch, "E200", {"start": v(59.95, 326.3) * mm, "end": v(62.2, 326.3) * mm, "construction": true});
            skLineSegment(sketch, "E201", {"start": v(-87.95, 326.3) * mm, "end": v(-90.2, 326.3) * mm, "construction": true});
            skCircle(sketch, "E202", {"center": v(-41.5, 283.8) * mm, "radius": 2.2 * mm});
            skCircle(sketch, "E203", {"center": v(13.5, 283.8) * mm, "radius": 2.2 * mm});
            skLineSegment(sketch, "E204", {"start": v(-41.5, 283.8) * mm, "end": v(13.5, 283.8) * mm, "construction": true});
            skLineSegment(sketch, "E205", {"start": v(-14, 290.1) * mm, "end": v(-14, 283.8) * mm, "construction": true});
            skLineSegment(sketch, "E206", {"start": v(-60.46, 304.8) * mm, "end": v(-38, 304.8) * mm, "construction": true});
            skLineSegment(sketch, "E207", {"start": v(-60.46, 314.8) * mm, "end": v(-60.46, 294.8) * mm, "construction": true});
            skLineSegment(sketch, "E208", {"start": v(-60.46, 294.8) * mm, "end": v(-60.46, 283.8) * mm, "construction": true});
            skLineSegment(sketch, "E209", {"start": v(18.35, 323.8) * mm, "end": v(18.35, 278.8) * mm});
            skLineSegment(sketch, "E210", {"start": v(-46.35, 323.8) * mm, "end": v(-46.35, 278.8) * mm});
            skLineSegment(sketch, "E211", {"start": v(-14, 323.8) * mm, "end": v(-14, 299.8) * mm, "construction": true});
            skLineSegment(sketch, "E212.bottom", {"start": v(-90.2, 323.8) * mm, "end": v(-86.2, 323.8) * mm});
            skLineSegment(sketch, "E212.top", {"start": v(-90.2, 333.8) * mm, "end": v(-86.2, 333.8) * mm});
            skLineSegment(sketch, "E212.left", {"start": v(-90.2, 323.8) * mm, "end": v(-90.2, 333.8) * mm});
            skLineSegment(sketch, "E212.right", {"start": v(-86.2, 323.8) * mm, "end": v(-86.2, 333.8) * mm});
            skLineSegment(sketch, "E213.bottom", {"start": v(62.2, 352.2) * mm, "end": v(58.2, 352.2) * mm});
            skLineSegment(sketch, "E213.top", {"start": v(62.2, 342.2) * mm, "end": v(58.2, 342.2) * mm});
            skLineSegment(sketch, "E213.left", {"start": v(62.2, 352.2) * mm, "end": v(62.2, 342.2) * mm});
            skLineSegment(sketch, "E213.right", {"start": v(58.2, 352.2) * mm, "end": v(58.2, 342.2) * mm});
            skSolve(sketch);
        }
        {
            var Q0;
            Q0=makeQuery(id+"F2.opExtrude","CAP_FACE",FACE,{"disambiguationData":[OSD([sQuery(id+"F1.wireOp",EDGE,"E0.bottom"),sQuery(id+"F1.wireOp",EDGE,"E0.top"),sQuery(id+"F1.wireOp",EDGE,"E0.left"),sQuery(id+"F1.wireOp",EDGE,"E0.right")])],"isStart":false});
            var sketch = newSketch(context, id + "F13", { "sketchPlane" : qUnion([Q0])});
            skLineSegment(sketch, "E214", {"start": v(26.25, 62.6) * mm, "end": v(24.25, 62.6) * mm});
            skArc(sketch, "E215", {"start": v(24.25, 62.6) * mm, "mid": v(23.05, 63.8) * mm, "end": v(24.25, 65) * mm});
            skArc(sketch, "E216", {"start": v(26.25, 62.6) * mm, "mid": v(27.45, 63.8) * mm, "end": v(26.25, 65) * mm});
            skLineSegment(sketch, "E217", {"start": v(26.25, 65) * mm, "end": v(24.25, 65) * mm});
            skLineSegment(sketch, "E218", {"start": v(25.25, 63.8) * mm, "end": v(25.25, 65) * mm, "construction": true});
            skLineSegment(sketch, "E219", {"start": v(26.25, 62.6) * mm, "end": v(26.25, 65) * mm, "construction": true});
            skLineSegment(sketch, "E220", {"start": v(24.25, 62.6) * mm, "end": v(24.25, 65) * mm, "construction": true});
            skLineSegment(sketch, "E221", {"start": v(-24.25, 62.6) * mm, "end": v(-26.25, 62.6) * mm});
            skArc(sketch, "E222", {"start": v(-26.25, 62.6) * mm, "mid": v(-27.45, 63.8) * mm, "end": v(-26.25, 65) * mm});
            skArc(sketch, "E223", {"start": v(-24.25, 62.6) * mm, "mid": v(-23.05, 63.8) * mm, "end": v(-24.25, 65) * mm});
            skLineSegment(sketch, "E224", {"start": v(-24.25, 65) * mm, "end": v(-26.25, 65) * mm});
            skLineSegment(sketch, "E225", {"start": v(-25.25, 63.8) * mm, "end": v(-25.25, 65) * mm, "construction": true});
            skLineSegment(sketch, "E226", {"start": v(-24.25, 62.6) * mm, "end": v(-24.25, 65) * mm, "construction": true});
            skLineSegment(sketch, "E227", {"start": v(-26.25, 62.6) * mm, "end": v(-26.25, 65) * mm, "construction": true});
            skCircle(sketch, "E228", {"center": v(-25.25, 63.8) * mm, "radius": 2.2 * mm});
            skCircle(sketch, "E229", {"center": v(25.25, 63.8) * mm, "radius": 2.2 * mm});
            skSolve(sketch);
        }
        {
            var Q0;
            Q0=makeQuery(id+"F12.imprint","IMPRINT",FACE,{"disambiguationData":[TD([[makeQuery(id+"F12.imprint","IMPRINT",EDGE,{"derivedFrom":sQuery(id+"F12.wireOp",EDGE,"E176")}),1.0]])]});
            extrude(context, id + "F14", {"entities" : qUnion([Q0]), "depth" : (getVariable(context, 'Mat_Thickness')) * mm});
        }
        {
            var Q0;
            Q0=qCreatedBy(makeId("Top.planeOp"),FACE);
            var sketch = newSketch(context, id + "F15", { "sketchPlane" : qUnion([Q0])});
            skLineSegment(sketch, "E230.top", {"start": v(-91.38, -76) * mm, "end": v(-166.38, -76) * mm});
            skLineSegment(sketch, "E230.left", {"start": v(-91.38, 45.4) * mm, "end": v(-91.38, -76) * mm});
            skLineSegment(sketch, "E230.right", {"start": v(-166.38, 45.4) * mm, "end": v(-166.38, -76) * mm});
            skLineSegment(sketch, "E231", {"start": v(-91.38, 0) * mm, "end": v(0, 0) * mm, "construction": true});
            skLineSegment(sketch, "E232", {"start": v(-166.38, 76) * mm, "end": v(-91.38, -76) * mm, "construction": true});
            skLineSegment(sketch, "E233", {"start": v(-166.38, -76) * mm, "end": v(-91.38, 76) * mm, "construction": true});
            skLineSegment(sketch, "E234.bottom", {"start": v(-101.38, 65) * mm, "end": v(-156.38, 65) * mm, "construction": true});
            skLineSegment(sketch, "E234.top", {"start": v(-101.38, -65) * mm, "end": v(-156.38, -65) * mm, "construction": true});
            skLineSegment(sketch, "E234.left", {"start": v(-101.38, 65) * mm, "end": v(-101.38, -65) * mm, "construction": true});
            skLineSegment(sketch, "E234.right", {"start": v(-156.38, 65) * mm, "end": v(-156.38, -65) * mm, "construction": true});
            skPoint(sketch, "E234.middle", {"position": v(-128.88, 0) * mm});
            skCircle(sketch, "E235", {"center": v(-101.38, -65) * mm, "radius": 2.2 * mm});
            skCircle(sketch, "E236", {"center": v(-156.38, -65) * mm, "radius": 2.2 * mm});
            skLineSegment(sketch, "E237", {"start": v(-166.38, 45.4) * mm, "end": v(-91.38, 45.4) * mm});
            skCircle(sketch, "E238", {"center": v(-156.38, -10) * mm, "radius": 2.2 * mm});
            skCircle(sketch, "E239", {"center": v(-156.38, 10) * mm, "radius": 2.2 * mm});
            skCircle(sketch, "E240", {"center": v(-101.38, -10) * mm, "radius": 2.2 * mm});
            skCircle(sketch, "E241", {"center": v(-101.38, 10) * mm, "radius": 2.2 * mm});
            skLineSegment(sketch, "E242", {"start": v(-101.38, 10) * mm, "end": v(-156.38, 10) * mm, "construction": true});
            skLineSegment(sketch, "E243", {"start": v(-101.38, -10) * mm, "end": v(-156.38, -10) * mm, "construction": true});
            skSolve(sketch);
        }
        {
            var Q0;
            Q0 = qSketchRegion(id + "F15", true);
            extrude(context, id + "F16", {"entities" : qUnion([Q0]), "depth" : (getVariable(context, 'Mat_Thickness')) * mm});
        }
        {
            var Q0;
            Q0=makeQuery(id+"F16.opExtrude","CAP_FACE",FACE,{"disambiguationData":[OSD([sQuery(id+"F15.wireOp",EDGE,"E230.bottom"),sQuery(id+"F15.wireOp",EDGE,"E230.top"),sQuery(id+"F15.wireOp",EDGE,"E230.left"),sQuery(id+"F15.wireOp",EDGE,"E230.right"),sQuery(id+"F15.wireOp",EDGE,"61G27m8L-Yme3-gyKG-xk8o-0eMGJO5fyKW1"),sQuery(id+"F15.wireOp",EDGE,"MFkOSKmS-Ay8l-Ns7G-jrVF-FJC99hM9UNIm"),sQuery(id+"F15.wireOp",EDGE,"E235"),sQuery(id+"F15.wireOp",EDGE,"E236")])],"isStart":false});
            var sketch = newSketch(context, id + "F17", { "sketchPlane" : qUnion([Q0])});
            skLineSegment(sketch, "E244.bottom", {"start": v(-104.6, -59.07) * mm, "end": v(-152.6, -59.07) * mm, "construction": true});
            skLineSegment(sketch, "E244.top", {"start": v(-104.6, 23.93) * mm, "end": v(-152.6, 23.93) * mm, "construction": true});
            skLineSegment(sketch, "E244.left", {"start": v(-104.6, -59.07) * mm, "end": v(-104.6, 23.93) * mm, "construction": true});
            skLineSegment(sketch, "E244.right", {"start": v(-152.6, -59.07) * mm, "end": v(-152.6, 23.93) * mm, "construction": true});
            skLineSegment(sketch, "E245", {"start": v(-152.6, 17.43) * mm, "end": v(-104.6, 17.43) * mm, "construction": true});
            skLineSegment(sketch, "E246", {"start": v(-152.6, -6.67) * mm, "end": v(-104.6, -6.67) * mm, "construction": true});
            skLineSegment(sketch, "E247", {"start": v(-152.6, -58.07) * mm, "end": v(-104.6, -58.07) * mm, "construction": true});
            skCircle(sketch, "E248", {"center": v(-104.6, 23.93) * mm, "radius": 2 * mm});
            skCircle(sketch, "E249", {"center": v(-152.6, 17.43) * mm, "radius": 2 * mm});
            skCircle(sketch, "E250", {"center": v(-137.6, -6.67) * mm, "radius": 2 * mm});
            skCircle(sketch, "E251", {"center": v(-109.6, -6.67) * mm, "radius": 2 * mm});
            skCircle(sketch, "E252", {"center": v(-152.6, -58.07) * mm, "radius": 2 * mm});
            skCircle(sketch, "E253", {"center": v(-104.6, -59.07) * mm, "radius": 2 * mm});
            skSolve(sketch);
        }
        {
            var Q0;
            Q0 = qSketchRegion(id + "F17", true);
            extrude(context, id + "F18", {"entities" : qUnion([Q0]), "operationType" : NewBodyOperationType.REMOVE, "oppositeDirection" : true, "depth" : 25 * mm});
        }
    });
